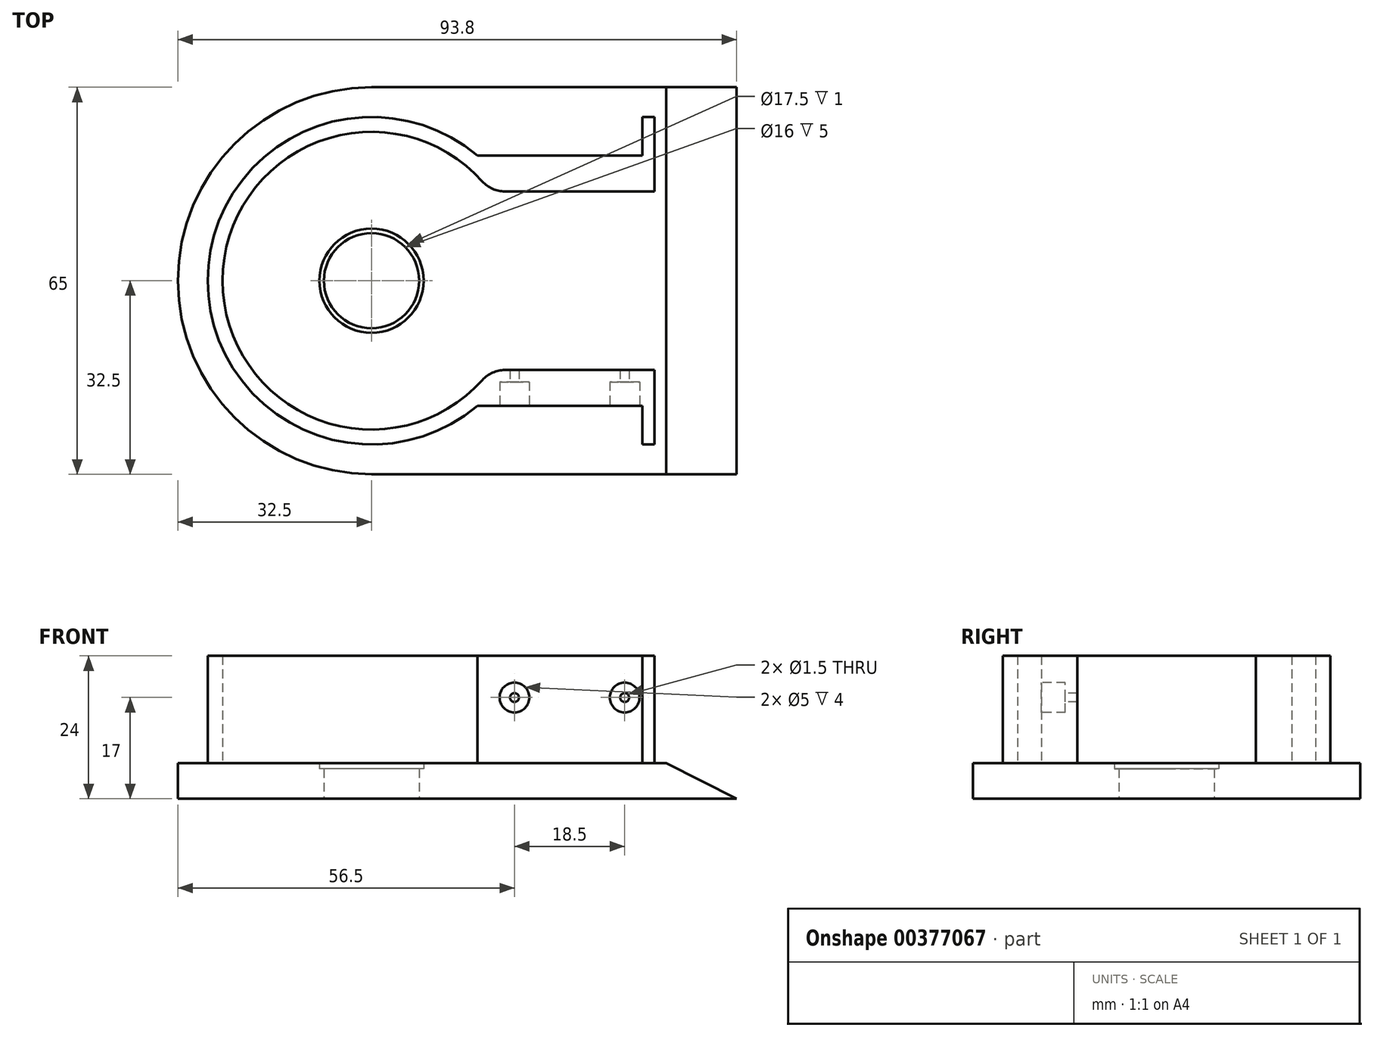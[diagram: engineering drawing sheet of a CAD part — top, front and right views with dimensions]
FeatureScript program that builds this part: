
annotation { "Feature Type Name" : "Feature", "Feature Type Description" : "" }
export const myFeature = defineFeature(function(context is Context, id is Id, definition is map)
    precondition{}
    {
        {
            var Q0;
            Q0=qCreatedBy(makeId("Top.planeOp"),FACE);
            var sketch = newSketch(context, id + "F0", { "sketchPlane" : qUnion([Q0])});
            skLineSegment(sketch, "E0.bottom", {"start": v(20, 15) * mm, "end": v(47.5, 15) * mm});
            skLineSegment(sketch, "E0.right", {"start": v(47.5, 15) * mm, "end": v(47.5, -15) * mm});
            skLineSegment(sketch, "E1", {"start": v(0, 0) * mm, "end": v(27.5, 0) * mm, "construction": true});
            skPoint(sketch, "E1.endSnap0", {"position": v(27.5, 0) * mm});
            skPoint(sketch, "E2.startSnap0", {"position": v(47.5, 0) * mm});
            skLineSegment(sketch, "E3", {"start": v(0, 27.5) * mm, "end": v(0, 27.5) * mm});
            skLineSegment(sketch, "E4", {"start": v(20, 15) * mm, "end": v(20, 15) * mm});
            skArc(sketch, "E5", {"start": v(20, -15) * mm, "mid": v(25, 0) * mm, "end": v(20, 15) * mm, "construction": true});
            skArc(sketch, "E6", {"start": v(20, 15) * mm, "mid": v(-25, 0) * mm, "end": v(20, -15) * mm});
            skArc(sketch, "E7", {"start": v(0, -27.5) * mm, "mid": v(5.24, -27) * mm, "end": v(10.3, -25.5) * mm});
            skArc(sketch, "E8", {"start": v(0, 27.5) * mm, "mid": v(-27.5, 0) * mm, "end": v(0, -27.5) * mm});
            skLineSegment(sketch, "E9", {"start": v(20, 15) * mm, "end": v(20, -15) * mm, "construction": true});
            skLineSegment(sketch, "E10", {"start": v(47.5, 27.5) * mm, "end": v(47.5, 15) * mm});
            skLineSegment(sketch, "E11", {"start": v(47.5, -15) * mm, "end": v(47.5, -27.5) * mm});
            skLineSegment(sketch, "E12", {"start": v(20, -15) * mm, "end": v(47.5, -15) * mm});
            skArc(sketch, "E13", {"start": v(17.76, -21) * mm, "mid": v(25.82, 9.45) * mm, "end": v(0, 27.5) * mm, "construction": true});
            skArc(sketch, "E14", {"start": v(10.3, -25.5) * mm, "mid": v(14.2, -23.55) * mm, "end": v(17.76, -21) * mm});
            skLineSegment(sketch, "E15", {"start": v(28, -17) * mm, "end": v(39.5, -17) * mm, "construction": true});
            skLineSegment(sketch, "E16", {"start": v(39.5, -17) * mm, "end": v(39.5, -21) * mm, "construction": true});
            skLineSegment(sketch, "E17", {"start": v(28, -17) * mm, "end": v(28, -21) * mm, "construction": true});
            skLineSegment(sketch, "E18", {"start": v(17.76, -21) * mm, "end": v(28, -21) * mm});
            skLineSegment(sketch, "E19", {"start": v(39.5, -21) * mm, "end": v(45.5, -21) * mm});
            skLineSegment(sketch, "E20.MirrorCS", {"start": v(17.76, 21) * mm, "end": v(28, 21) * mm});
            skLineSegment(sketch, "E21.MirrorCS", {"start": v(28, 17) * mm, "end": v(28, 21) * mm, "construction": true});
            skLineSegment(sketch, "E22.MirrorCS", {"start": v(28, 17) * mm, "end": v(39.5, 17) * mm, "construction": true});
            skLineSegment(sketch, "E23.MirrorCS", {"start": v(39.5, 17) * mm, "end": v(39.5, 21) * mm, "construction": true});
            skLineSegment(sketch, "E24.MirrorCS", {"start": v(39.5, 21) * mm, "end": v(45.5, 21) * mm});
            skArc(sketch, "E25.MirrorCS", {"start": v(10.3, 25.5) * mm, "mid": v(14.2, 23.55) * mm, "end": v(17.76, 21) * mm});
            skLineSegment(sketch, "E26", {"start": v(45.5, -21) * mm, "end": v(45.5, -27.5) * mm});
            skLineSegment(sketch, "E27", {"start": v(47.5, -27.5) * mm, "end": v(45.5, -27.5) * mm});
            skLineSegment(sketch, "E28", {"start": v(45.5, -27.5) * mm, "end": v(0, -27.5) * mm});
            skLineSegment(sketch, "E29.MirrorCS", {"start": v(45.5, 21) * mm, "end": v(45.5, 27.5) * mm});
            skLineSegment(sketch, "E30.MirrorCS", {"start": v(47.5, 27.5) * mm, "end": v(45.5, 27.5) * mm});
            skLineSegment(sketch, "E31.MirrorCS", {"start": v(45.5, 27.5) * mm, "end": v(0, 27.5) * mm});
            skArc(sketch, "E32.MirrorCS", {"start": v(0, 27.5) * mm, "mid": v(5.24, 27) * mm, "end": v(10.3, 25.5) * mm});
            skLineSegment(sketch, "E33", {"start": v(47.5, 27.5) * mm, "end": v(49.5, 27.5) * mm});
            skLineSegment(sketch, "E34", {"start": v(49.5, 27.5) * mm, "end": v(49.5, -27.5) * mm});
            skLineSegment(sketch, "E35", {"start": v(49.5, -27.5) * mm, "end": v(47.5, -27.5) * mm});
            skLineSegment(sketch, "E36", {"start": v(0, 32.5) * mm, "end": v(49.5, 32.5) * mm});
            skLineSegment(sketch, "E37", {"start": v(49.5, 32.5) * mm, "end": v(49.5, 27.5) * mm});
            skLineSegment(sketch, "E38.MirrorCS", {"start": v(0, -32.5) * mm, "end": v(49.5, -32.5) * mm});
            skLineSegment(sketch, "E39.MirrorCS", {"start": v(49.5, -32.5) * mm, "end": v(49.5, -27.5) * mm});
            skArc(sketch, "E40", {"start": v(0, 32.5) * mm, "mid": v(-32.5, 0) * mm, "end": v(0, -32.5) * mm});
            skArc(sketch, "E41", {"start": v(0, -32.5) * mm, "mid": v(32.5, 0) * mm, "end": v(0, 32.5) * mm, "construction": true});
            skLineSegment(sketch, "E42", {"start": v(28, 21) * mm, "end": v(39.5, 21) * mm});
            skLineSegment(sketch, "E43", {"start": v(28, -21) * mm, "end": v(39.5, -21) * mm});
            skCircle(sketch, "E44", {"center": v(0, 0) * mm, "radius": 8 * mm});
            skCircle(sketch, "E45", {"center": v(0, 0) * mm, "radius": 8.75 * mm});
            skSolve(sketch);
        }
        {
            var Q0;
            Q0=makeQuery(id+"F0.imprint","IMPRINT",FACE,{"disambiguationData":[TD([[makeQuery(id+"F0.imprint","IMPRINT",EDGE,{"derivedFrom":sQuery(id+"F0.wireOp",EDGE,"E0.bottom")}),1.0]])]});
            extrude(context, id + "F1", {"entities" : qUnion([Q0]), "offsetDistance" : 25 * mm, "depth" : 24 * mm});
        }
        {
            var Q0;
            Q0=makeQuery(id+"F0.imprint","IMPRINT",FACE,{"disambiguationData":[TD([[makeQuery(id+"F0.imprint","IMPRINT",EDGE,{"derivedFrom":sQuery(id+"F0.wireOp",EDGE,"E0.bottom")}),-1.0]])]});
            var Q1;
            Q1=makeQuery(id+"F0.imprint","IMPRINT",FACE,{"disambiguationData":[TD([[makeQuery(id+"F0.imprint","IMPRINT",EDGE,{"derivedFrom":sQuery(id+"F0.wireOp",EDGE,"E20.MirrorCS")}),1.0]])]});
            var Q2;
            Q2=makeQuery(id+"F0.imprint","IMPRINT",FACE,{"disambiguationData":[TD([[makeQuery(id+"F0.imprint","IMPRINT",EDGE,{"derivedFrom":sQuery(id+"F0.wireOp",EDGE,"E7")}),-1.0]])]});
            var Q3;
            Q3=makeQuery(id+"F0.imprint","IMPRINT",FACE,{"disambiguationData":[TD([[makeQuery(id+"F0.imprint","IMPRINT",EDGE,{"derivedFrom":sQuery(id+"F0.wireOp",EDGE,"E0.right")}),1.0]])]});
            var Q4;
            Q4=makeQuery(id+"F0.imprint","IMPRINT",FACE,{"disambiguationData":[TD([[makeQuery(id+"F0.imprint","IMPRINT",EDGE,{"derivedFrom":sQuery(id+"F0.wireOp",EDGE,"E8")}),-1.0]])]});
            extrude(context, id + "F2", {"entities" : qUnion([Q0, Q1, Q2, Q3, Q4]), "operationType" : NewBodyOperationType.ADD, "offsetDistance" : 25 * mm, "depth" : 6 * mm});
        }
        {
            var Q0;
            Q0=qCreatedBy(makeId("Front.planeOp"),FACE);
            var sketch = newSketch(context, id + "F3", { "sketchPlane" : qUnion([Q0])});
            skPoint(sketch, "E46.0", {"position": v(49.5, 0) * mm});
            skLineSegment(sketch, "E47", {"start": v(49.5, 0) * mm, "end": v(61.3, 0) * mm});
            skPoint(sketch, "E48.0", {"position": v(49.5, 6) * mm});
            skLineSegment(sketch, "E49", {"start": v(49.5, 6) * mm, "end": v(61.3, 0) * mm});
            skLineSegment(sketch, "E50", {"start": v(49.5, 0) * mm, "end": v(49.5, 6) * mm});
            skSolve(sketch);
        }
        {
            var Q0;
            Q0=makeQuery(id+"F3.imprint","IMPRINT",FACE,{"disambiguationData":[TD([[makeQuery(id+"F3.imprint","IMPRINT",EDGE,{"derivedFrom":sQuery(id+"F3.wireOp",EDGE,"E47")}),1.0]])]});
            extrude(context, id + "F4", {"entities" : qUnion([Q0]), "operationType" : NewBodyOperationType.ADD, "depth" : 65 * mm, "symmetric" : true});
        }
        {
            var Q0;
            Q0=makeQuery(id+"F1.opExtrude","SWEPT_EDGE",EDGE,{"disambiguationData":[OSD([sQuery(id+"F0.wireOp",EDGE,"E0.bottom"),sQuery(id+"F0.wireOp",EDGE,"E6")])]});
            var Q1;
            Q1=makeQuery(id+"F1.opExtrude","SWEPT_EDGE",EDGE,{"disambiguationData":[OSD([sQuery(id+"F0.wireOp",EDGE,"E6"),sQuery(id+"F0.wireOp",EDGE,"E12")])]});
            fillet(context, id + "F5", {"entities" : qUnion([Q0, Q1]), "radius" : 5 * mm, "tangentPropagation" : true, "allowEdgeOverflow" : false});
        }
        {
            var Q0;
            Q0=makeQuery(id+"F1.opExtrude","SWEPT_FACE",FACE,{"disambiguationData":[OSD([sQuery(id+"F0.wireOp",EDGE,"E18")])]});
            var sketch = newSketch(context, id + "F6", { "sketchPlane" : qUnion([Q0])});
            skPoint(sketch, "E51.0", {"position": v(28, 24) * mm});
            skLineSegment(sketch, "E52", {"start": v(28, 24) * mm, "end": v(24, 24) * mm, "construction": true});
            skLineSegment(sketch, "E53", {"start": v(24, 24) * mm, "end": v(24, 17) * mm, "construction": true});
            skCircle(sketch, "E54", {"center": v(24, 17) * mm, "radius": 0.75 * mm});
            skCircle(sketch, "E55", {"center": v(24, 17) * mm, "radius": 2.5 * mm});
            skCircle(sketch, "E56", {"center": v(42.5, 17) * mm, "radius": 0.75 * mm});
            skCircle(sketch, "E57", {"center": v(42.5, 17) * mm, "radius": 2.5 * mm});
            skPoint(sketch, "E58.5", {"position": v(45.5, 24) * mm});
            skLineSegment(sketch, "E59", {"start": v(42.5, 24) * mm, "end": v(42.5, 17) * mm, "construction": true});
            skLineSegment(sketch, "E60", {"start": v(45.5, 24) * mm, "end": v(42.5, 24) * mm});
            skSolve(sketch);
        }
        {
            var Q0;
            Q0=makeQuery(id+"F6.imprint","IMPRINT",FACE,{"disambiguationData":[TD([[makeQuery(id+"F6.imprint","IMPRINT",EDGE,{"derivedFrom":sQuery(id+"F6.wireOp",EDGE,"E54")}),1.0]])]});
            var Q1;
            Q1=makeQuery(id+"F6.imprint","IMPRINT",FACE,{"disambiguationData":[TD([[makeQuery(id+"F6.imprint","IMPRINT",EDGE,{"derivedFrom":sQuery(id+"F6.wireOp",EDGE,"E56")}),1.0]])]});
            extrude(context, id + "F7", {"entities" : qUnion([Q0, Q1]), "operationType" : NewBodyOperationType.REMOVE, "endBound" : BoundingType.UP_TO_NEXT, "oppositeDirection" : true, "depth" : 10 * mm});
        }
        {
            var Q0;
            Q0=makeQuery(id+"F6.imprint","IMPRINT",FACE,{"disambiguationData":[TD([[makeQuery(id+"F6.imprint","IMPRINT",EDGE,{"derivedFrom":sQuery(id+"F6.wireOp",EDGE,"E54")}),-1.0]])]});
            var Q1;
            Q1=makeQuery(id+"F6.imprint","IMPRINT",FACE,{"disambiguationData":[TD([[makeQuery(id+"F6.imprint","IMPRINT",EDGE,{"derivedFrom":sQuery(id+"F6.wireOp",EDGE,"E56")}),-1.0]])]});
            extrude(context, id + "F8", {"entities" : qUnion([Q0, Q1]), "operationType" : NewBodyOperationType.REMOVE, "oppositeDirection" : true, "depth" : 4 * mm});
        }
        {
            var Q0;
            Q0=makeQuery(id+"F0.imprint","IMPRINT",FACE,{"disambiguationData":[TD([[makeQuery(id+"F0.imprint","IMPRINT",EDGE,{"derivedFrom":sQuery(id+"F0.wireOp",EDGE,"E44")}),-1.0]])]});
            extrude(context, id + "F9", {"entities" : qUnion([Q0]), "operationType" : NewBodyOperationType.ADD, "depth" : 5 * mm, "offsetDistance" : 25 * mm});
        }
    });
